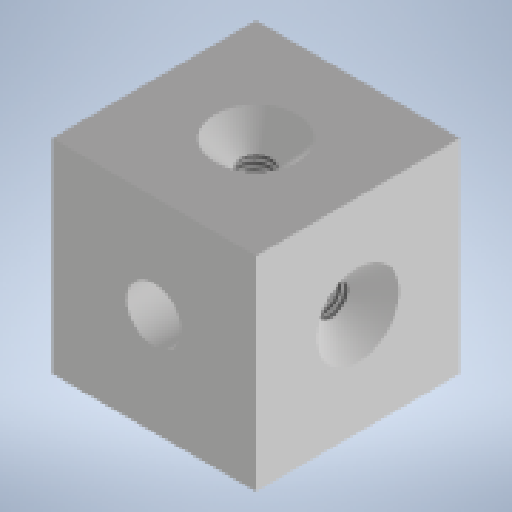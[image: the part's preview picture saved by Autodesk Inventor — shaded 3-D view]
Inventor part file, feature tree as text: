
AUTODESK INVENTOR PART (.ipt)
format: ipt  version: 2025 (Build 290162010, 162A)  size: 163,328 bytes
history: native  units: mm
features: sketch x4, hole x3, extrude x1
ambient origin geometry x8: Origin, YZ Plane, XZ Plane, XY Plane, X Axis, Y Axis, Z Axis, Center Point
bodies: Volumenkörper1 (feature_tree)
feature tree (8):
  extrude  "Extrusion1"  Depth=16.0mm
  hole  "Bohrung1"  [1 undecoded]
  hole  "Bohrung2"  [1 undecoded]
  hole  "Bohrung3"  [1 undecoded]
  sketch  "Skizze1"  dims[d0=16.0mm d1=16.0mm]
  sketch  "Skizze2"  dims[d2=16.0mm d3=0.0mm d4=5.0mm]
  sketch  "Skizze3"  dims[d5=4.3mm d6=6.0mm d7=11.0mm d8=2.0mm d9=90.0deg d10=8.0mm d11=20.594885mm d12=8.0mm]
  sketch  "Skizze4"  dims[d13=2.459mm d14=6.0mm d15=11.0mm d16=2.0mm d17=90.0deg d18=8.0mm d19=20.594885mm d20=8.0mm d21=2.459mm d22=6.0mm d23=4.0mm d24=2.0mm d25=90.0deg d26=8.0mm d27=20.594885mm]
note: 3 required parameter values undecoded (feature->parameter linkage not recoverable at this tier; creation-order binding heuristic only, values carry confidence <= 0.55)
